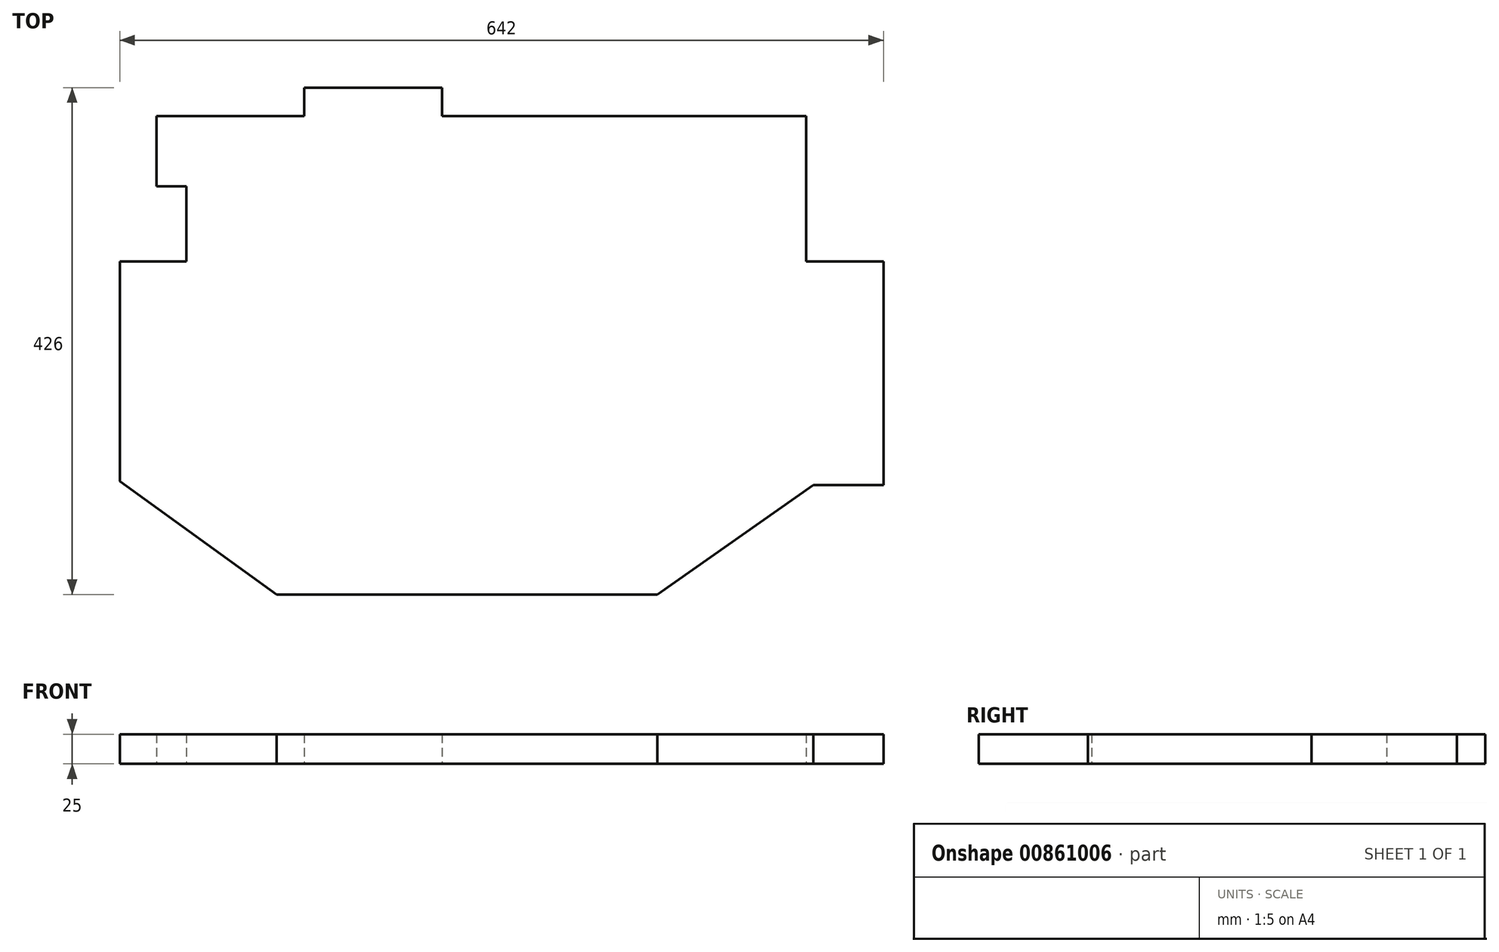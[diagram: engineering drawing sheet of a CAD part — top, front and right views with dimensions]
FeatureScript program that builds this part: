
annotation { "Feature Type Name" : "Feature", "Feature Type Description" : "" }
export const myFeature = defineFeature(function(context is Context, id is Id, definition is map)
    precondition{}
    {
        {
            var Q0;
            Q0=qCreatedBy(makeId("Top.planeOp"),FACE);
            var sketch = newSketch(context, id + "F0", { "sketchPlane" : qUnion([Q0])});
            skLineSegment(sketch, "E0", {"start": v(-546, 0) * mm, "end": v(-422, 0) * mm});
            skLineSegment(sketch, "E1", {"start": v(0, 0) * mm, "end": v(0, -122) * mm});
            skLineSegment(sketch, "E2", {"start": v(0, -122) * mm, "end": v(65, -122) * mm});
            skLineSegment(sketch, "E3", {"start": v(65, -122) * mm, "end": v(65, -310) * mm});
            skLineSegment(sketch, "E4", {"start": v(65, -310) * mm, "end": v(6, -310) * mm});
            skLineSegment(sketch, "E5", {"start": v(0, -122) * mm, "end": v(-521, -122) * mm, "construction": true});
            skLineSegment(sketch, "E6", {"start": v(-521, -122) * mm, "end": v(-521, -304) * mm, "construction": true});
            skLineSegment(sketch, "E7", {"start": v(26.16, 0) * mm, "end": v(26.16, -402) * mm, "construction": true});
            skLineSegment(sketch, "E8", {"start": v(-445, -402) * mm, "end": v(-125, -402) * mm});
            skLineSegment(sketch, "E9", {"start": v(6, -310) * mm, "end": v(-125, -402) * mm});
            skLineSegment(sketch, "E10", {"start": v(65, -175.44) * mm, "end": v(-583, -175.44) * mm, "construction": true});
            skLineSegment(sketch, "E11", {"start": v(-546, 0) * mm, "end": v(-546, -59) * mm});
            skLineSegment(sketch, "E12", {"start": v(-546, -122) * mm, "end": v(-577, -122) * mm});
            skLineSegment(sketch, "E13", {"start": v(-577, -122) * mm, "end": v(-577, -307) * mm});
            skLineSegment(sketch, "E14", {"start": v(-577, -307) * mm, "end": v(-445, -402) * mm});
            skLineSegment(sketch, "E15", {"start": v(-546, -122) * mm, "end": v(-521, -122) * mm});
            skLineSegment(sketch, "E16", {"start": v(-521, -122) * mm, "end": v(-521, -59) * mm});
            skLineSegment(sketch, "E17", {"start": v(-521, -59) * mm, "end": v(-546, -59) * mm});
            skLineSegment(sketch, "E18", {"start": v(-273, 0) * mm, "end": v(-273, -402) * mm, "construction": true});
            skLineSegment(sketch, "E19", {"start": v(0, 0) * mm, "end": v(-306, 0) * mm});
            skLineSegment(sketch, "E20", {"start": v(-306, 0) * mm, "end": v(-306, 24) * mm});
            skLineSegment(sketch, "E21", {"start": v(-306, 24) * mm, "end": v(-422, 24) * mm});
            skLineSegment(sketch, "E22", {"start": v(-422, 24) * mm, "end": v(-422, 0) * mm});
            skLineSegment(sketch, "E23.trimOffspring", {"start": v(-306, 0) * mm, "end": v(0, 0) * mm});
            skText(sketch, "E24", { "text": "4 x 138", "fontName": "OpenSans-Regular.ttf"});
            skText(sketch, "E25", { "text": "34 x 148", "fontName": "OpenSans-Regular.ttf"});
            skLineSegment(sketch, "E26.direction1", {"start": v(-14.8, 0) * mm, "end": v(-29.6, 0) * mm, "construction": true});
            skLineSegment(sketch, "E27.direction1", {"start": v(14.8, -122) * mm, "end": v(29.6, -122) * mm, "construction": true});
            skPoint(sketch, "E28", {"position": v(65, -147.57) * mm});
            skPoint(sketch, "E29.1.0.0", {"position": v(50.2, -147.57) * mm});
            skPoint(sketch, "E29.2.0.0", {"position": v(35.4, -147.57) * mm});
            skPoint(sketch, "E29.3.0.0", {"position": v(20.6, -147.57) * mm});
            skPoint(sketch, "E29.4.0.0", {"position": v(5.8, -147.57) * mm});
            skPoint(sketch, "E29.5.0.0", {"position": v(-9, -147.57) * mm});
            skPoint(sketch, "E29.6.0.0", {"position": v(-23.8, -147.57) * mm});
            skPoint(sketch, "E29.7.0.0", {"position": v(-38.6, -147.57) * mm});
            skPoint(sketch, "E29.8.0.0", {"position": v(-53.4, -147.57) * mm});
            skPoint(sketch, "E29.9.0.0", {"position": v(-68.2, -147.57) * mm});
            skPoint(sketch, "E29.10.0.0", {"position": v(-83, -147.57) * mm});
            skPoint(sketch, "E29.11.0.0", {"position": v(-97.8, -147.57) * mm});
            skPoint(sketch, "E29.12.0.0", {"position": v(-112.6, -147.57) * mm});
            skPoint(sketch, "E29.13.0.0", {"position": v(-127.4, -147.57) * mm});
            skPoint(sketch, "E29.14.0.0", {"position": v(-142.2, -147.57) * mm});
            skPoint(sketch, "E29.15.0.0", {"position": v(-157, -147.57) * mm});
            skPoint(sketch, "E29.16.0.0", {"position": v(-171.8, -147.57) * mm});
            skPoint(sketch, "E29.17.0.0", {"position": v(-186.6, -147.57) * mm});
            skPoint(sketch, "E29.18.0.0", {"position": v(-201.4, -147.57) * mm});
            skPoint(sketch, "E29.19.0.0", {"position": v(-216.2, -147.57) * mm});
            skPoint(sketch, "E29.20.0.0", {"position": v(-231, -147.57) * mm});
            skPoint(sketch, "E29.21.0.0", {"position": v(-245.8, -147.57) * mm});
            skPoint(sketch, "E29.22.0.0", {"position": v(-260.6, -147.57) * mm});
            skPoint(sketch, "E29.23.0.0", {"position": v(-275.4, -147.57) * mm});
            skPoint(sketch, "E29.24.0.0", {"position": v(-290.2, -147.57) * mm});
            skPoint(sketch, "E29.25.0.0", {"position": v(-305, -147.57) * mm});
            skPoint(sketch, "E29.26.0.0", {"position": v(-319.8, -147.57) * mm});
            skPoint(sketch, "E29.27.0.0", {"position": v(-334.6, -147.57) * mm});
            skPoint(sketch, "E29.28.0.0", {"position": v(-349.4, -147.57) * mm});
            skPoint(sketch, "E29.29.0.0", {"position": v(-364.2, -147.57) * mm});
            skPoint(sketch, "E29.30.0.0", {"position": v(-379, -147.57) * mm});
            skPoint(sketch, "E29.31.0.0", {"position": v(-393.8, -147.57) * mm});
            skPoint(sketch, "E29.32.0.0", {"position": v(-408.6, -147.57) * mm});
            skPoint(sketch, "E29.33.0.0", {"position": v(-423.4, -147.57) * mm});
            skPoint(sketch, "E29.34.0.0", {"position": v(-438.2, -147.57) * mm});
            skPoint(sketch, "E29.35.0.0", {"position": v(-453, -147.57) * mm});
            skPoint(sketch, "E29.36.0.0", {"position": v(-467.8, -147.57) * mm});
            skPoint(sketch, "E29.37.0.0", {"position": v(-482.6, -147.57) * mm});
            skPoint(sketch, "E29.38.0.0", {"position": v(-497.4, -147.57) * mm});
            skPoint(sketch, "E29.39.0.0", {"position": v(-512.2, -147.57) * mm});
            skPoint(sketch, "E29.40.0.0", {"position": v(-527, -147.57) * mm});
            skPoint(sketch, "E29.41.0.0", {"position": v(-541.8, -147.57) * mm});
            skPoint(sketch, "E29.42.0.0", {"position": v(-556.6, -147.57) * mm});
            skPoint(sketch, "E29.43.0.0", {"position": v(-571.4, -147.57) * mm});
            skPoint(sketch, "E29.44.0.0", {"position": v(-586.2, -147.57) * mm});
            skLineSegment(sketch, "E29.direction1", {"start": v(65, -147.57) * mm, "end": v(50.2, -147.57) * mm, "construction": true});
            skLineSegment(sketch, "E30", {"start": v(-306, 0) * mm, "end": v(-305, -211.87) * mm, "construction": true});
            skLineSegment(sketch, "E31", {"start": v(50.2, -122) * mm, "end": v(50.2, -310) * mm, "construction": true});
            skLineSegment(sketch, "E32", {"start": v(35.4, -122) * mm, "end": v(35.4, -310) * mm, "construction": true});
            skLineSegment(sketch, "E33", {"start": v(20.6, -122) * mm, "end": v(20.6, -310) * mm, "construction": true});
            skLineSegment(sketch, "E34", {"start": v(5.8, -122) * mm, "end": v(6, -310) * mm, "construction": true});
            skLineSegment(sketch, "E35", {"start": v(-9, 0) * mm, "end": v(-9, -320.53) * mm, "construction": true});
            skLineSegment(sketch, "E36", {"start": v(-23.8, 0) * mm, "end": v(-23.8, -330.93) * mm, "construction": true});
            skLineSegment(sketch, "E37", {"start": v(-38.6, 0) * mm, "end": v(-38.6, -341.32) * mm, "construction": true});
            skLineSegment(sketch, "E38", {"start": v(-53.4, 0) * mm, "end": v(-53.4, -351.72) * mm, "construction": true});
            skLineSegment(sketch, "E39", {"start": v(-68.2, 0) * mm, "end": v(-68.2, -362.1) * mm, "construction": true});
            skLineSegment(sketch, "E40", {"start": v(-83, 0) * mm, "end": v(-83, -372.5) * mm, "construction": true});
            skLineSegment(sketch, "E41", {"start": v(-97.8, 0) * mm, "end": v(-97.8, -382.9) * mm, "construction": true});
            skLineSegment(sketch, "E42", {"start": v(-112.6, 0) * mm, "end": v(-112.6, -393.3) * mm, "construction": true});
            skLineSegment(sketch, "E43", {"start": v(-127.4, 0) * mm, "end": v(-127.4, -402) * mm, "construction": true});
            skLineSegment(sketch, "E44", {"start": v(-306, 0) * mm, "end": v(-304.1, -402) * mm});
            skLineSegment(sketch, "E45", {"start": v(-319.8, 24) * mm, "end": v(-319.8, -402) * mm, "construction": true});
            skLineSegment(sketch, "E46", {"start": v(-423.4, 0) * mm, "end": v(-423.4, -402) * mm, "construction": true});
            skLineSegment(sketch, "E47", {"start": v(-438.2, 0) * mm, "end": v(-438.2, -402) * mm, "construction": true});
            skLineSegment(sketch, "E48", {"start": v(-453, 0) * mm, "end": v(-453, -396.24) * mm, "construction": true});
            skLineSegment(sketch, "E49", {"start": v(-467.8, 0) * mm, "end": v(-467.8, -385.6) * mm, "construction": true});
            skLineSegment(sketch, "E50", {"start": v(-482.6, 0) * mm, "end": v(-482.6, -374.94) * mm, "construction": true});
            skLineSegment(sketch, "E51", {"start": v(-497.4, 0) * mm, "end": v(-497.4, -364.29) * mm, "construction": true});
            skLineSegment(sketch, "E52", {"start": v(-512.2, 0) * mm, "end": v(-512.2, -353.64) * mm, "construction": true});
            skLineSegment(sketch, "E53", {"start": v(-527, 0) * mm, "end": v(-527, -342.98) * mm, "construction": true});
            skLineSegment(sketch, "E54", {"start": v(-541.8, -122) * mm, "end": v(-541.8, -332.33) * mm, "construction": true});
            skPoint(sketch, "E55", {"position": v(-527, -122) * mm});
            skLineSegment(sketch, "E56", {"start": v(-556.6, -122) * mm, "end": v(-556.6, -321.68) * mm, "construction": true});
            skLineSegment(sketch, "E57", {"start": v(-571.4, -122) * mm, "end": v(-571.4, -311.03) * mm, "construction": true});
            skPoint(sketch, "E58", {"position": v(-364, -6) * mm});
            skPoint(sketch, "E58.positionSnap0", {"position": v(-364, 24) * mm});
            skPoint(sketch, "E59.0.1.0", {"position": v(-364, -66) * mm});
            skPoint(sketch, "E59.0.2.0", {"position": v(-364, -126) * mm});
            skPoint(sketch, "E59.0.3.0", {"position": v(-364, -186) * mm});
            skPoint(sketch, "E59.0.4.0", {"position": v(-364, -246) * mm});
            skPoint(sketch, "E59.0.5.0", {"position": v(-364, -306) * mm});
            skPoint(sketch, "E59.0.6.0", {"position": v(-364, -366) * mm});
            skPoint(sketch, "E59.0.7.0", {"position": v(-364, -426) * mm});
            skLineSegment(sketch, "E59.direction1", {"start": v(-364, -6) * mm, "end": v(-339, -6) * mm, "construction": true});
            skLineSegment(sketch, "E59.direction2", {"start": v(-364, -6) * mm, "end": v(-364, -66) * mm, "construction": true});
            skLineSegment(sketch, "E60", {"start": v(-546, -6) * mm, "end": v(0, -6) * mm});
            skLineSegment(sketch, "E61", {"start": v(-521, -66) * mm, "end": v(0, -66) * mm});
            skLineSegment(sketch, "E62", {"start": v(-577, -126) * mm, "end": v(65, -126) * mm});
            skLineSegment(sketch, "E63", {"start": v(-577, -186) * mm, "end": v(65, -186) * mm});
            skLineSegment(sketch, "E64", {"start": v(-577, -246) * mm, "end": v(65, -246) * mm});
            skLineSegment(sketch, "E65", {"start": v(65, -306) * mm, "end": v(-571.4, -306) * mm});
            skLineSegment(sketch, "E66", {"start": v(-73.74, -366) * mm, "end": v(-495.02, -366) * mm});
            const initialGuessF0  = {"E24": [0.10035, -0.11613, 1, 0, 0.02208], "E25": [-0.69831, -0.20036, 1, 0, 0.01893]};
            skSetInitialGuess(sketch, initialGuessF0);
            skSolve(sketch);
        }
        {
            var Q0;
            Q0=qCreatedBy(makeId("Right.planeOp"),FACE);
            var sketch = newSketch(context, id + "F1", { "sketchPlane" : qUnion([Q0])});
            skLineSegment(sketch, "E67", {"start": v(0, 0) * mm, "end": v(0, 546) * mm});
            skLineSegment(sketch, "E68", {"start": v(0, 0) * mm, "end": v(-113, 0) * mm});
            skLineSegment(sketch, "E69", {"start": v(-113, 0) * mm, "end": v(-113, 522) * mm});
            skLineSegment(sketch, "E70", {"start": v(-56.5, 546) * mm, "end": v(0, 546) * mm});
            skLineSegment(sketch, "E71", {"start": v(-56.5, 546) * mm, "end": v(-56.5, 522) * mm});
            skLineSegment(sketch, "E72", {"start": v(-56.5, 522) * mm, "end": v(-113, 522) * mm});
            skPoint(sketch, "E73", {"position": v(-14.8, 0) * mm});
            skPoint(sketch, "E74.1.0.0", {"position": v(-29.6, 0) * mm});
            skPoint(sketch, "E74.2.0.0", {"position": v(-44.4, 0) * mm});
            skPoint(sketch, "E74.3.0.0", {"position": v(-59.2, 0) * mm});
            skPoint(sketch, "E74.4.0.0", {"position": v(-74, 0) * mm});
            skPoint(sketch, "E74.5.0.0", {"position": v(-88.8, 0) * mm});
            skPoint(sketch, "E74.6.0.0", {"position": v(-103.6, 0) * mm});
            skLineSegment(sketch, "E74.direction1", {"start": v(-14.8, 0) * mm, "end": v(-29.6, 0) * mm, "construction": true});
            skText(sketch, "E75", { "text": "+2 x 150 => 1x305", "fontName": "OpenSans-Regular.ttf"});
            skLineSegment(sketch, "E76", {"start": v(-14.8, 0) * mm, "end": v(-14.8, 546) * mm, "construction": true});
            skLineSegment(sketch, "E77", {"start": v(-29.6, 0) * mm, "end": v(-29.6, 546) * mm, "construction": true});
            skLineSegment(sketch, "E78", {"start": v(-44.4, 0) * mm, "end": v(-44.4, 546) * mm, "construction": true});
            skLineSegment(sketch, "E79", {"start": v(-59.2, 0) * mm, "end": v(-59.2, 522) * mm, "construction": true});
            skLineSegment(sketch, "E80", {"start": v(-74, 0) * mm, "end": v(-74, 522) * mm, "construction": true});
            skLineSegment(sketch, "E81", {"start": v(-88.8, 0) * mm, "end": v(-88.8, 522) * mm, "construction": true});
            skLineSegment(sketch, "E82", {"start": v(-103.6, 0) * mm, "end": v(-103.6, 522) * mm, "construction": true});
            const initialGuessF1  = {"E75": [0.00737, 0.3233, 1, 0, 0.05004]};
            skSetInitialGuess(sketch, initialGuessF1);
            skSolve(sketch);
        }
        {
            var Q0;
            Q0=qCreatedBy(makeId("Top.planeOp"),FACE);
            var sketch = newSketch(context, id + "F2", { "sketchPlane" : qUnion([Q0])});
            skLineSegment(sketch, "E83.0", {"start": v(-546, 0) * mm, "end": v(-422, 0) * mm});
            skLineSegment(sketch, "E84.0", {"start": v(-422, 24) * mm, "end": v(-422, 0) * mm});
            skLineSegment(sketch, "E85.0", {"start": v(-306, 24) * mm, "end": v(-422, 24) * mm});
            skLineSegment(sketch, "E86.0", {"start": v(-306, 0) * mm, "end": v(-306, 24) * mm});
            skLineSegment(sketch, "E87.0", {"start": v(-306, 0) * mm, "end": v(0, 0) * mm});
            skLineSegment(sketch, "E88.0", {"start": v(0, 0) * mm, "end": v(0, -113) * mm});
            skLineSegment(sketch, "E89.0", {"start": v(0, 0) * mm, "end": v(0, -122) * mm});
            skLineSegment(sketch, "E90.0", {"start": v(0, -122) * mm, "end": v(65, -122) * mm});
            skLineSegment(sketch, "E91.0", {"start": v(65, -122) * mm, "end": v(65, -310) * mm});
            skLineSegment(sketch, "E92.0", {"start": v(65, -310) * mm, "end": v(6, -310) * mm});
            skLineSegment(sketch, "E93.0", {"start": v(6, -310) * mm, "end": v(-125, -402) * mm});
            skLineSegment(sketch, "E94.0", {"start": v(-445, -402) * mm, "end": v(-125, -402) * mm});
            skLineSegment(sketch, "E95.0", {"start": v(-577, -307) * mm, "end": v(-445, -402) * mm});
            skLineSegment(sketch, "E96.0", {"start": v(-577, -122) * mm, "end": v(-577, -307) * mm});
            skLineSegment(sketch, "E97.0", {"start": v(-546, -122) * mm, "end": v(-577, -122) * mm});
            skLineSegment(sketch, "E98.0", {"start": v(-546, -122) * mm, "end": v(-521, -122) * mm});
            skLineSegment(sketch, "E99.0", {"start": v(-521, -122) * mm, "end": v(-521, -59) * mm});
            skLineSegment(sketch, "E100.0", {"start": v(-521, -59) * mm, "end": v(-546, -59) * mm});
            skLineSegment(sketch, "E101.0", {"start": v(-546, 0) * mm, "end": v(-546, -59) * mm});
            skSolve(sketch);
        }
        {
            var Q0;
            Q0 = qSketchRegion(id + "F2", true);
            extrude(context, id + "F3", {"entities" : qUnion([Q0]), "depth" : 25 * mm, "offsetDistance" : 25 * mm});
        }
    });
